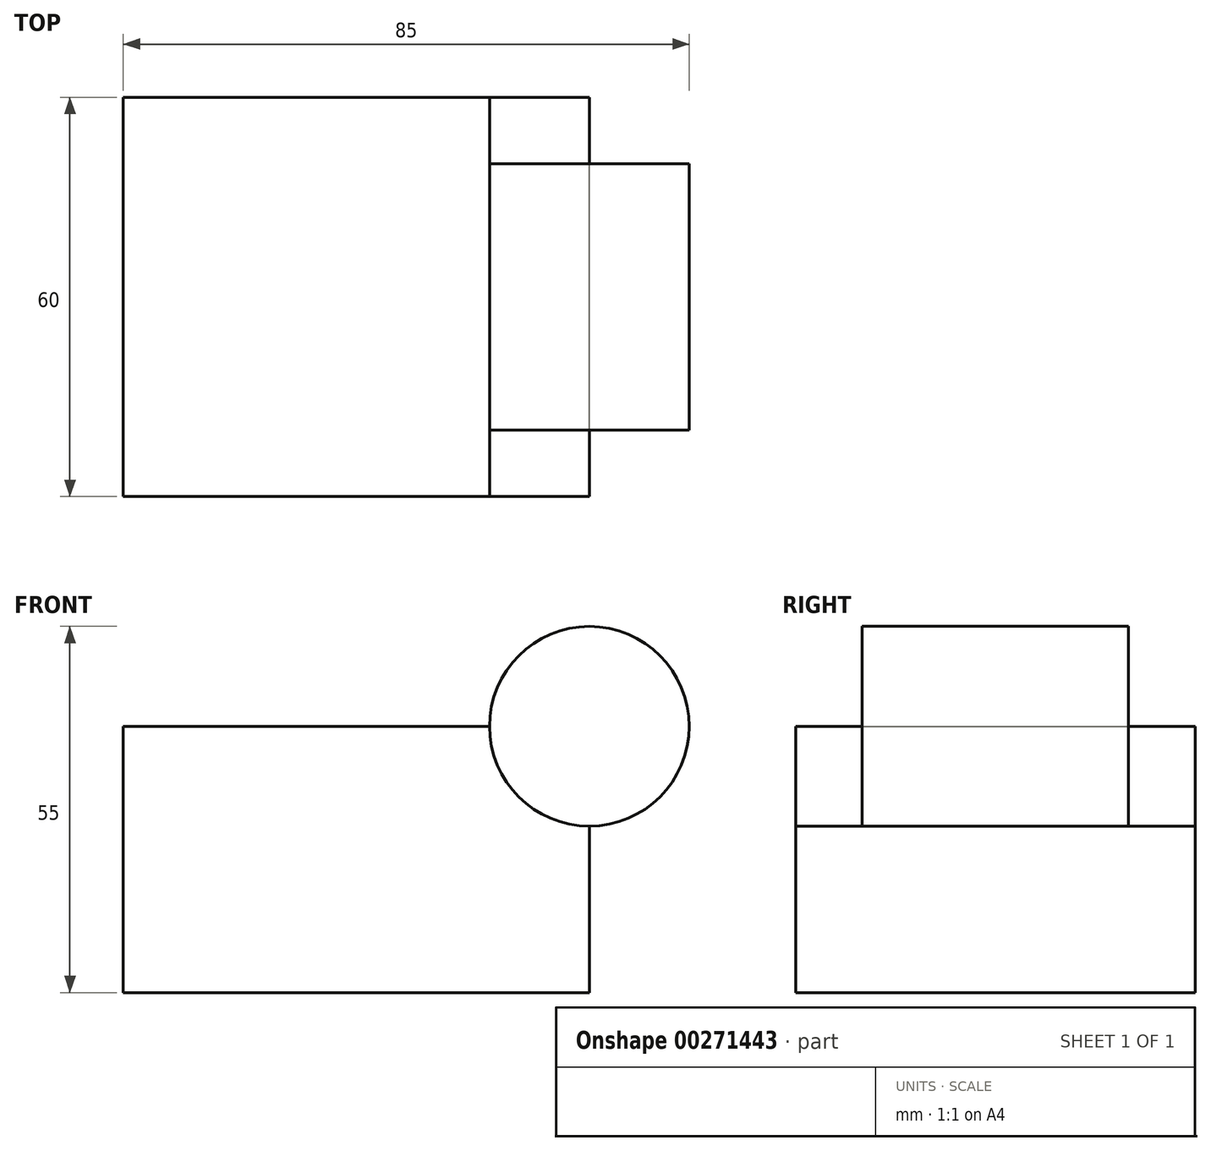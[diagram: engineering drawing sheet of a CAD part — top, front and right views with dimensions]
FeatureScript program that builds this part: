
annotation { "Feature Type Name" : "Feature", "Feature Type Description" : "" }
export const myFeature = defineFeature(function(context is Context, id is Id, definition is map)
    precondition{}
    {
        {
            var Q0;
            Q0=qCreatedBy(makeId("Front.planeOp"),FACE);
            var sketch = newSketch(context, id + "F0", { "sketchPlane" : qUnion([Q0])});
            skLineSegment(sketch, "E0.bottom", {"start": v(35, 20) * mm, "end": v(-35, 20) * mm});
            skLineSegment(sketch, "E0.top", {"start": v(35, -20) * mm, "end": v(-35, -20) * mm});
            skLineSegment(sketch, "E0.left", {"start": v(35, 20) * mm, "end": v(35, -20) * mm});
            skLineSegment(sketch, "E0.right", {"start": v(-35, 20) * mm, "end": v(-35, -20) * mm});
            skPoint(sketch, "E0.middle", {"position": v(0, 0) * mm});
            skCircle(sketch, "E1", {"center": v(35, 20) * mm, "radius": 15 * mm});
            skSolve(sketch);
        }
        {
            var Q0;
            {var subQ2=sQuery(id+"F0.wireOp",EDGE,"E0.top");Q0=makeQuery(id+"F0.imprint","IMPRINT",FACE,{"disambiguationData":[TD([[makeQuery(id+"F0.imprint","IMPRINT",EDGE,{"derivedFrom":subQ2}),-1.0]])]});}
            extrude(context, id + "F1", {"entities" : qUnion([Q0]), "endBound" : BoundingType.SYMMETRIC, "depth" : 20 * mm});
        }
        {
            var Q0;
            Q0 = qSketchRegion(id + "F0", true);
            var Q1;
            Q1=makeQuery(id+"F1.opExtrude","CAP_FACE",FACE,{"disambiguationData":[OSD([sQuery(id+"F0.wireOp",EDGE,"E0.bottom"),sQuery(id+"F0.wireOp",EDGE,"E0.top"),sQuery(id+"F0.wireOp",EDGE,"E0.left"),sQuery(id+"F0.wireOp",EDGE,"E0.right"),sQuery(id+"F0.wireOp",EDGE,"E1")])],"isStart":false});
            extrude(context, id + "F2", {"entities" : qUnion([Q0, Q1]), "operationType" : NewBodyOperationType.ADD, "depth" : 40 * mm});
        }
    });
